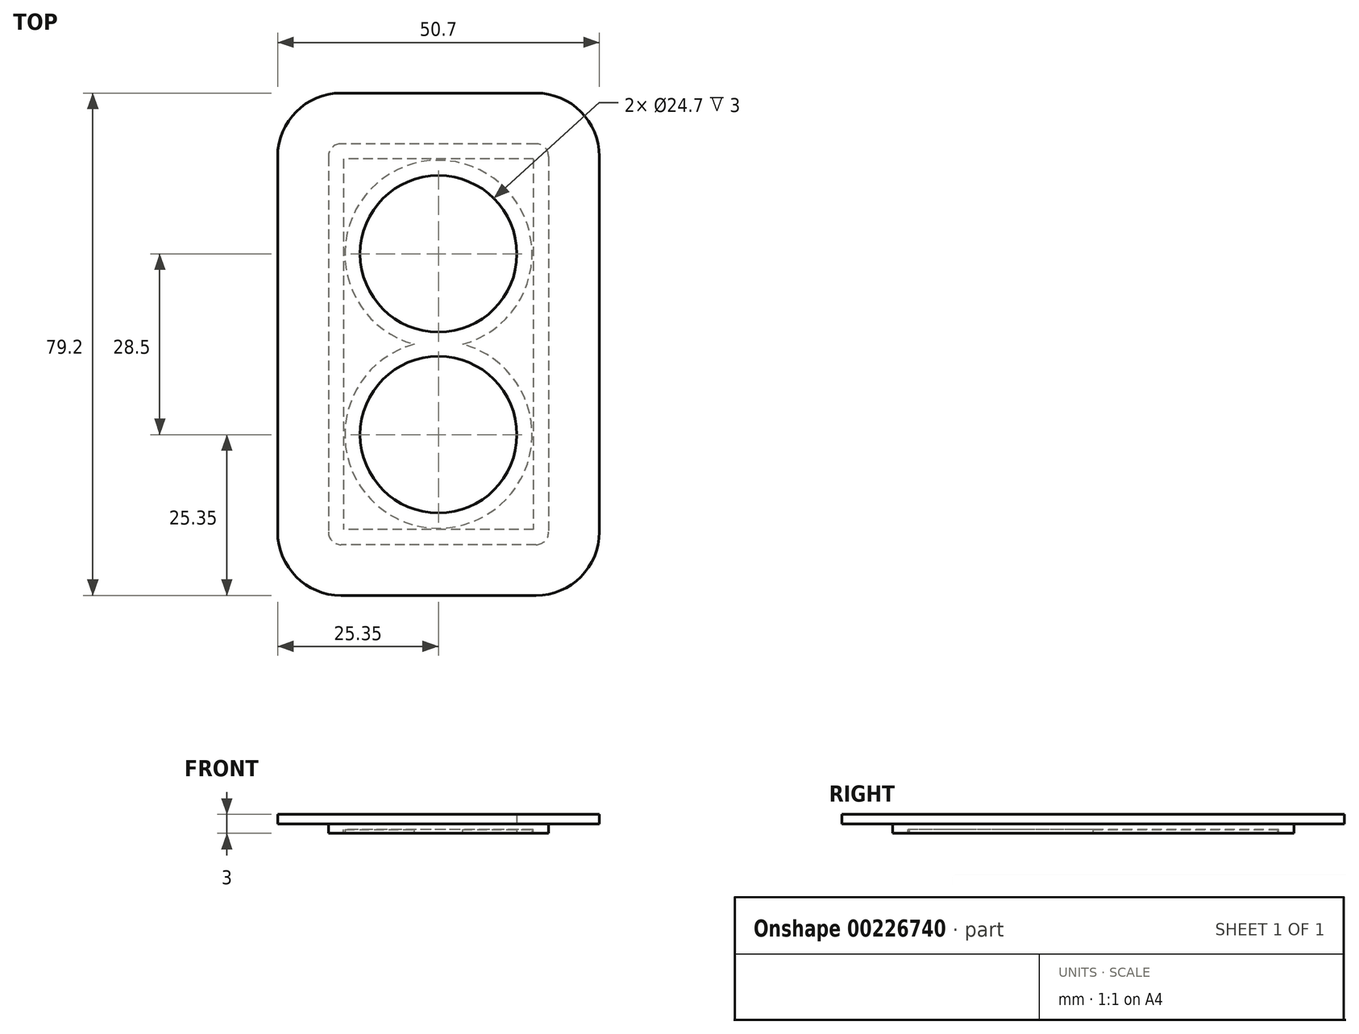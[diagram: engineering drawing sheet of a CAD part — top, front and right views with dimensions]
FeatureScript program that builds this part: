
annotation { "Feature Type Name" : "Feature", "Feature Type Description" : "" }
export const myFeature = defineFeature(function(context is Context, id is Id, definition is map)
    precondition{}
    {
        {
            var Q0;
            Q0=qCreatedBy(makeId("Top.planeOp"),FACE);
            var sketch = newSketch(context, id + "F0", { "sketchPlane" : qUnion([Q0])});
            skLineSegment(sketch, "E0.bottom", {"start": v(17.35, 31.6) * mm, "end": v(-17.35, 31.6) * mm});
            skLineSegment(sketch, "E0.top", {"start": v(17.35, -31.6) * mm, "end": v(-17.35, -31.6) * mm});
            skLineSegment(sketch, "E0.left", {"start": v(17.35, 31.6) * mm, "end": v(17.35, -31.6) * mm});
            skLineSegment(sketch, "E0.right", {"start": v(-17.35, 31.6) * mm, "end": v(-17.35, -31.6) * mm});
            skPoint(sketch, "E0.middle", {"position": v(0, 0) * mm});
            skCircle(sketch, "E1", {"center": v(0, 14.25) * mm, "radius": 12.35 * mm});
            skCircle(sketch, "E2.0.1.0", {"center": v(0, -14.25) * mm, "radius": 12.35 * mm});
            skLineSegment(sketch, "E2.direction1", {"start": v(0, 14.25) * mm, "end": v(28.5, 14.25) * mm, "construction": true});
            skLineSegment(sketch, "E2.direction2", {"start": v(0, 14.25) * mm, "end": v(0, -14.25) * mm, "construction": true});
            skSolve(sketch);
        }
        {
            var Q0;
            Q0 = qSketchRegion(id + "F0", true);
            extrude(context, id + "F1", {"entities" : qUnion([Q0]), "depth" : 3 * mm});
        }
        {
            var Q0;
            Q0=makeQuery(id+"F1.opExtrude","SWEPT_EDGE",EDGE,{"disambiguationData":[OSD([sQuery(id+"F0.wireOp",EDGE,"E0.bottom"),sQuery(id+"F0.wireOp",EDGE,"E0.right")])]});
            var Q1;
            Q1=makeQuery(id+"F1.opExtrude","SWEPT_EDGE",EDGE,{"disambiguationData":[OSD([sQuery(id+"F0.wireOp",EDGE,"E0.top"),sQuery(id+"F0.wireOp",EDGE,"E0.right")])]});
            var Q2;
            Q2=makeQuery(id+"F1.opExtrude","SWEPT_EDGE",EDGE,{"disambiguationData":[OSD([sQuery(id+"F0.wireOp",EDGE,"E0.top"),sQuery(id+"F0.wireOp",EDGE,"E0.left")])]});
            var Q3;
            Q3=makeQuery(id+"F1.opExtrude","SWEPT_EDGE",EDGE,{"disambiguationData":[OSD([sQuery(id+"F0.wireOp",EDGE,"E0.bottom"),sQuery(id+"F0.wireOp",EDGE,"E0.left")])]});
            fillet(context, id + "F2", {"entities" : qUnion([Q0, Q1, Q2, Q3]), "radius" : 2 * mm, "tangentPropagation" : true, "allowEdgeOverflow" : false});
        }
        {
            var Q0;
            Q0=makeQuery(id+"F1.opExtrude","CAP_FACE",FACE,{"disambiguationData":[OSD([sQuery(id+"F0.wireOp",EDGE,"E0.bottom"),sQuery(id+"F0.wireOp",EDGE,"E0.top"),sQuery(id+"F0.wireOp",EDGE,"E0.left"),sQuery(id+"F0.wireOp",EDGE,"E0.right"),sQuery(id+"F0.wireOp",EDGE,"E1"),sQuery(id+"F0.wireOp",EDGE,"E2.0.1.0"),sQuery(id+"F0.wireOp",EDGE,"E2.1.0.0"),sQuery(id+"F0.wireOp",EDGE,"E2.1.1.0"),sQuery(id+"F0.wireOp",EDGE,"E2.2.0.0"),sQuery(id+"F0.wireOp",EDGE,"E2.2.1.0")])],"isStart":true});
            shell(context, id + "F3", {"entities" : qUnion([Q0]), "thickness" : 2.4 * mm});
        }
        {
            var Q0;
            Q0=makeQuery(id+"F1.opExtrude","CAP_FACE",FACE,{"disambiguationData":[OSD([sQuery(id+"F0.wireOp",EDGE,"E0.bottom"),sQuery(id+"F0.wireOp",EDGE,"E0.top"),sQuery(id+"F0.wireOp",EDGE,"E0.left"),sQuery(id+"F0.wireOp",EDGE,"E0.right"),sQuery(id+"F0.wireOp",EDGE,"E1"),sQuery(id+"F0.wireOp",EDGE,"E2.0.1.0"),sQuery(id+"F0.wireOp",EDGE,"E2.1.0.0"),sQuery(id+"F0.wireOp",EDGE,"E2.1.1.0"),sQuery(id+"F0.wireOp",EDGE,"E2.2.0.0"),sQuery(id+"F0.wireOp",EDGE,"E2.2.1.0")])],"isStart":false});
            var sketch = newSketch(context, id + "F4", { "sketchPlane" : qUnion([Q0])});
            skArc(sketch, "E3.0", {"start": v(25.35, 29.6) * mm, "mid": v(22.42, 36.67) * mm, "end": v(15.35, 39.6) * mm});
            skLineSegment(sketch, "E3.1", {"start": v(25.35, 29.6) * mm, "end": v(25.35, -29.6) * mm});
            skLineSegment(sketch, "E3.2", {"start": v(15.35, 39.6) * mm, "end": v(-15.35, 39.6) * mm});
            skArc(sketch, "E3.3", {"start": v(15.35, -39.6) * mm, "mid": v(22.42, -36.67) * mm, "end": v(25.35, -29.6) * mm});
            skArc(sketch, "E3.4", {"start": v(-15.35, 39.6) * mm, "mid": v(-22.42, 36.67) * mm, "end": v(-25.35, 29.6) * mm});
            skLineSegment(sketch, "E3.5", {"start": v(-25.35, 29.6) * mm, "end": v(-25.35, -29.6) * mm});
            skArc(sketch, "E3.6", {"start": v(-25.35, -29.6) * mm, "mid": v(-22.42, -36.67) * mm, "end": v(-15.35, -39.6) * mm});
            skLineSegment(sketch, "E3.7", {"start": v(15.35, -39.6) * mm, "end": v(-15.35, -39.6) * mm});
            skCircle(sketch, "E4.0", {"center": v(0, 14.25) * mm, "radius": 12.35 * mm});
            skCircle(sketch, "E5.0", {"center": v(0, -14.25) * mm, "radius": 12.35 * mm});
            skSolve(sketch);
        }
        {
            var Q0;
            Q0 = qSketchRegion(id + "F4", true);
            extrude(context, id + "F5", {"entities" : qUnion([Q0]), "operationType" : NewBodyOperationType.ADD, "oppositeDirection" : true, "depth" : 1.5 * mm});
        }
    });
